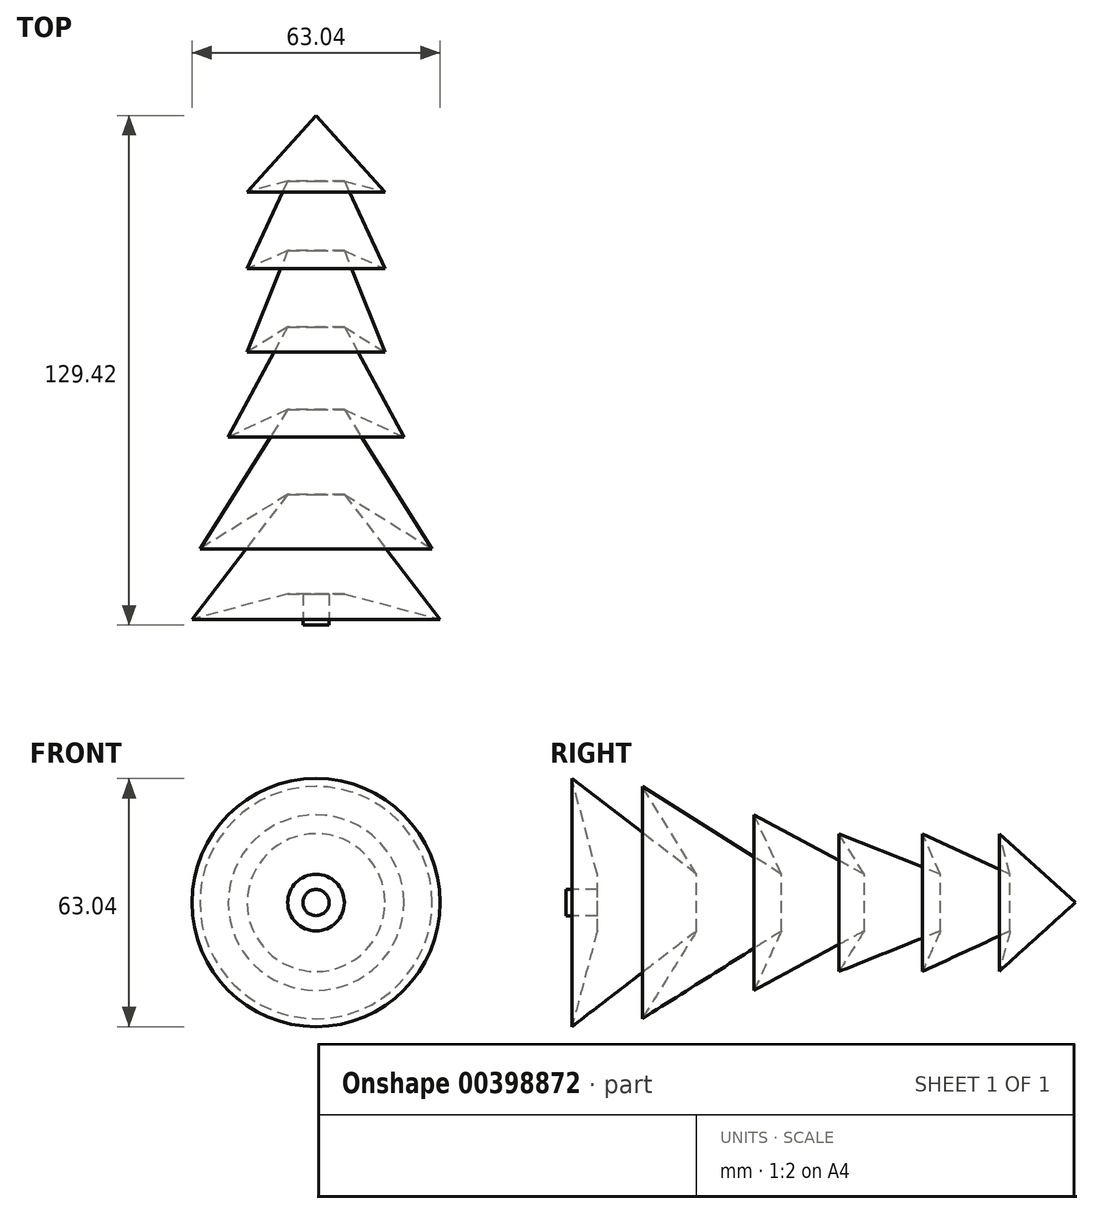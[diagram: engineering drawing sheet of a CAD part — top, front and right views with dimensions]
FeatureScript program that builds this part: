
annotation { "Feature Type Name" : "Feature", "Feature Type Description" : "" }
export const myFeature = defineFeature(function(context is Context, id is Id, definition is map)
    precondition{}
    {
        {
            var Q0;
            Q0=qCreatedBy(makeId("Top.planeOp"),FACE);
            var sketch = newSketch(context, id + "F0", { "sketchPlane" : qUnion([Q0])});
            skLineSegment(sketch, "E0", {"start": v(0, 53.65) * mm, "end": v(17.51, 34.3) * mm});
            skLineSegment(sketch, "E1", {"start": v(17.51, 34.3) * mm, "end": v(7.19, 37.06) * mm});
            skLineSegment(sketch, "E2", {"start": v(7.19, 37.06) * mm, "end": v(17.51, 14.75) * mm});
            skLineSegment(sketch, "E3", {"start": v(17.51, 14.75) * mm, "end": v(7.19, 19.36) * mm});
            skLineSegment(sketch, "E4", {"start": v(7.19, 19.36) * mm, "end": v(17.51, -6.45) * mm});
            skLineSegment(sketch, "E5", {"start": v(17.51, -6.45) * mm, "end": v(7.19, 0) * mm});
            skLineSegment(sketch, "E6", {"start": v(7.19, 0) * mm, "end": v(22.3, -28.02) * mm});
            skLineSegment(sketch, "E7", {"start": v(22.3, -28.02) * mm, "end": v(7.19, -21.02) * mm});
            skLineSegment(sketch, "E8", {"start": v(7.19, -21.02) * mm, "end": v(29.5, -56.41) * mm});
            skLineSegment(sketch, "E9", {"start": v(29.5, -56.41) * mm, "end": v(7.19, -42.59) * mm});
            skLineSegment(sketch, "E10", {"start": v(7.19, -42.59) * mm, "end": v(31.52, -74.3) * mm});
            skLineSegment(sketch, "E11", {"start": v(31.52, -74.3) * mm, "end": v(7.19, -67.84) * mm});
            skLineSegment(sketch, "E12", {"start": v(7.19, -67.84) * mm, "end": v(3.32, -67.84) * mm});
            skLineSegment(sketch, "E13", {"start": v(3.32, -67.84) * mm, "end": v(3.32, -75.77) * mm});
            skLineSegment(sketch, "E14", {"start": v(3.32, -75.77) * mm, "end": v(0, -75.77) * mm});
            skLineSegment(sketch, "E15", {"start": v(0, -75.77) * mm, "end": v(0, 53.65) * mm});
            skSolve(sketch);
        }
        {
            var Q0;
            Q0 = qSketchRegion(id + "F0", true);
            var Q1;
            Q1=sQuery(id+"F0.wireOp",EDGE,"E15");
            revolve(context, id + "F1", {"entities" : qUnion([Q0]), "axis" : qUnion([Q1]), "revolveType" : RevolveType.FULL});
        }
    });
